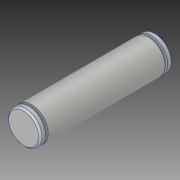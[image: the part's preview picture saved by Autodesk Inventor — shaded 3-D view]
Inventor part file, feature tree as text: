
AUTODESK INVENTOR PART (.ipt)
format: ipt  version: 2018.2 (Build 222227000, 227)  size: 239,616 bytes
history: native  units: mm
features: other x5, chamfer x1, sketch x1
ambient origin geometry x8: Origin, YZ Plane, XZ Plane, XY Plane, X Axis, Y Axis, Z Axis, Center Point
bodies: Body1 (feature_tree), Body2 (feature_tree)
feature tree (7):
  other  "200-40-BOGIE-CONNECTOR-01.ipt"
  other  "Grundkörper"
  chamfer  "Fase1"  Distance=20.0mm
  other  "Bezeichnung2"
  sketch  "Skizze6"  dims[d40=10.0mm d41=20.0mm d43=1.55mm d46=20.0mm d47=90.0deg d48=1.0mm d49=2.0mm d50=45.0deg d51=15.0mm d54=5.0mm d57=0.25mm]
  other  "Volumenkörper1::200-40-BOGIE-CONNECTOR-01.ipt"
  other  "Flä2"
